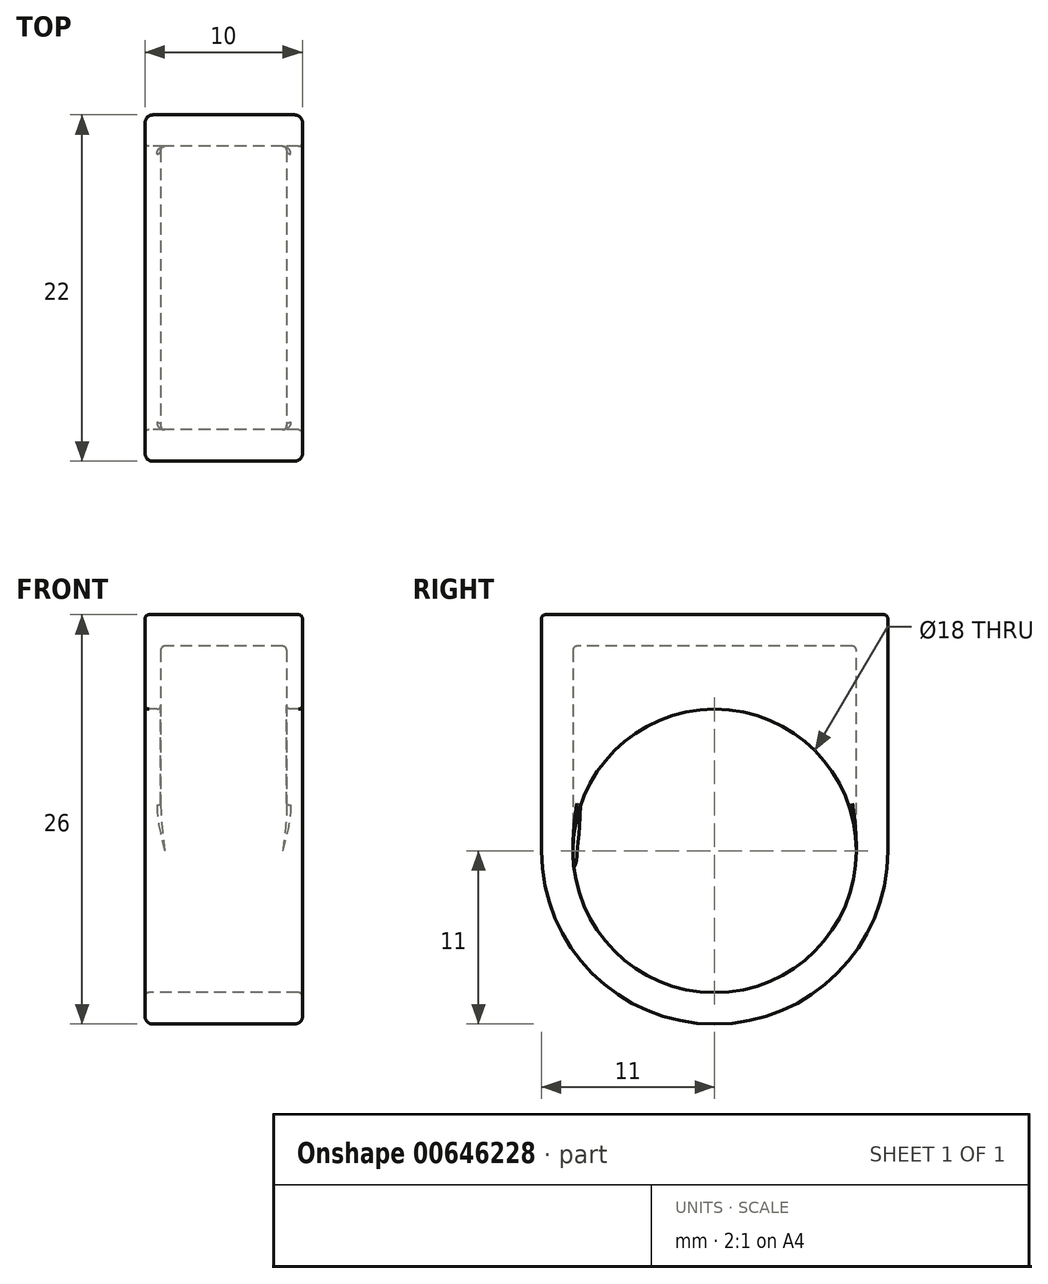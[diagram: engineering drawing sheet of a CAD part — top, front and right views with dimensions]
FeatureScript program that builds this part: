
annotation { "Feature Type Name" : "Feature", "Feature Type Description" : "" }
export const myFeature = defineFeature(function(context is Context, id is Id, definition is map)
    precondition{}
    {
        {
            var Q0;
            Q0=qCreatedBy(makeId("Right.planeOp"),FACE);
            var sketch = newSketch(context, id + "F0", { "sketchPlane" : qUnion([Q0])});
            skCircle(sketch, "E0", {"center": v(0, 0) * mm, "radius": 9 * mm});
            skArc(sketch, "E1", {"start": v(-11, 0) * mm, "mid": v(0, -11) * mm, "end": v(11, 0) * mm});
            skLineSegment(sketch, "E2", {"start": v(-11, 0) * mm, "end": v(-11, 15) * mm});
            skLineSegment(sketch, "E3", {"start": v(11, 0) * mm, "end": v(11, 15) * mm});
            skLineSegment(sketch, "E4", {"start": v(-11, 15) * mm, "end": v(11, 15) * mm});
            skSolve(sketch);
        }
        {
            var Q0;
            Q0 = qSketchRegion(id + "F0", true);
            extrude(context, id + "F1", {"entities" : qUnion([Q0]), "endBound" : BoundingType.SYMMETRIC, "depth" : 10 * mm, "offsetDistance" : 25 * mm});
        }
        {
            var Q0;
            Q0=qCreatedBy(makeId("Right.planeOp"),FACE);
            var sketch = newSketch(context, id + "F2", { "sketchPlane" : qUnion([Q0])});
            skLineSegment(sketch, "E5.0", {"start": v(9, 13) * mm, "end": v(-9, 13) * mm});
            skLineSegment(sketch, "E5.1", {"start": v(9, 0) * mm, "end": v(9, 13) * mm});
            skArc(sketch, "E5.2", {"start": v(-9, 0) * mm, "mid": v(0, -9) * mm, "end": v(9, 0) * mm});
            skLineSegment(sketch, "E5.3", {"start": v(-9, 13) * mm, "end": v(-9, 0) * mm});
            skSolve(sketch);
        }
        {
            var Q0;
            Q0 = qSketchRegion(id + "F2", true);
            extrude(context, id + "F3", {"entities" : qUnion([Q0]), "operationType" : NewBodyOperationType.REMOVE, "endBound" : BoundingType.SYMMETRIC, "depth" : 8 * mm, "offsetDistance" : 25 * mm});
        }
        {
            var Q0;
            Q0=makeQuery(id+"F1.opExtrude","CAP_EDGE",EDGE,{"disambiguationData":[OSD([sQuery(id+"F0.wireOp",EDGE,"E2")])],"isStart":true});
            var Q1;
            Q1=makeQuery(id+"F1.opExtrude","CAP_EDGE",EDGE,{"disambiguationData":[OSD([sQuery(id+"F0.wireOp",EDGE,"E2")])],"isStart":false});
            fillet(context, id + "F4", {"entities" : qUnion([Q0, Q1]), "radius" : 0.5 * mm, "tangentPropagation" : true, "allowEdgeOverflow" : false});
        }
        {
            var Q0;
            Q0=makeQuery(id+"F1.opExtrude","CAP_EDGE",EDGE,{"disambiguationData":[OSD([sQuery(id+"F0.wireOp",EDGE,"E0")])],"isStart":false});
            var Q1;
            Q1=makeQuery(id+"F1.opExtrude","CAP_FACE",FACE,{"disambiguationData":[OSD([sQuery(id+"F0.wireOp",EDGE,"E0"),sQuery(id+"F0.wireOp",EDGE,"E1"),sQuery(id+"F0.wireOp",EDGE,"E2"),sQuery(id+"F0.wireOp",EDGE,"E3"),sQuery(id+"F0.wireOp",EDGE,"E4")])],"isStart":false});
            var Q2;
            Q2=makeQuery(id+"F1.opExtrude","CAP_FACE",FACE,{"disambiguationData":[OSD([sQuery(id+"F0.wireOp",EDGE,"E0"),sQuery(id+"F0.wireOp",EDGE,"E1"),sQuery(id+"F0.wireOp",EDGE,"E2"),sQuery(id+"F0.wireOp",EDGE,"E3"),sQuery(id+"F0.wireOp",EDGE,"E4")])],"isStart":true});
            var Q3;
            Q3=makeQuery(id+"F1.opExtrude","SWEPT_FACE",FACE,{"disambiguationData":[OSD([sQuery(id+"F0.wireOp",EDGE,"E2")])]});
            var Q4;
            Q4=makeQuery(id+"F1.opExtrude","SWEPT_EDGE",EDGE,{"disambiguationData":[OSD([sQuery(id+"F0.wireOp",EDGE,"E3"),sQuery(id+"F0.wireOp",EDGE,"E4")])]});
            var Q5;
            Q5=makeQuery(id+"F1.opExtrude","SWEPT_EDGE",EDGE,{"disambiguationData":[OSD([sQuery(id+"F0.wireOp",EDGE,"E1"),sQuery(id+"F0.wireOp",EDGE,"E2")])]});
            var Q6;
            Q6=makeQuery(id+"F1.opExtrude","SWEPT_EDGE",EDGE,{"disambiguationData":[OSD([sQuery(id+"F0.wireOp",EDGE,"E2"),sQuery(id+"F0.wireOp",EDGE,"E4")])]});
            var Q7;
            Q7=makeQuery(id+"F1.opExtrude","CAP_EDGE",EDGE,{"disambiguationData":[OSD([sQuery(id+"F0.wireOp",EDGE,"E4")])],"isStart":false});
            var Q8;
            Q8=makeQuery(id+"F1.opExtrude","CAP_EDGE",EDGE,{"disambiguationData":[OSD([sQuery(id+"F0.wireOp",EDGE,"E0")])],"isStart":true});
            var Q9;
            Q9=makeQuery(id+"F1.opExtrude","SWEPT_FACE",FACE,{"disambiguationData":[OSD([sQuery(id+"F0.wireOp",EDGE,"E1")])]});
            var Q10;
            Q10=makeQuery(id+"F1.opExtrude","SWEPT_FACE",FACE,{"disambiguationData":[OSD([sQuery(id+"F0.wireOp",EDGE,"E3")])]});
            var Q11;
            Q11=makeQuery(id+"F1.opExtrude","CAP_EDGE",EDGE,{"disambiguationData":[OSD([sQuery(id+"F0.wireOp",EDGE,"E1")])],"isStart":true});
            var Q12;
            Q12=makeQuery(id+"F1.opExtrude","SWEPT_FACE",FACE,{"disambiguationData":[OSD([sQuery(id+"F0.wireOp",EDGE,"E4")])]});
            var Q13;
            Q13=makeQuery(id+"F1.opExtrude","CAP_EDGE",EDGE,{"disambiguationData":[OSD([sQuery(id+"F0.wireOp",EDGE,"E1")])],"isStart":false});
            var Q14;
            Q14=makeQuery(id+"F1.opExtrude","CAP_EDGE",EDGE,{"disambiguationData":[OSD([sQuery(id+"F0.wireOp",EDGE,"E2")])],"isStart":true});
            var Q15;
            Q15=makeQuery(id+"F1.opExtrude","CAP_EDGE",EDGE,{"disambiguationData":[OSD([sQuery(id+"F0.wireOp",EDGE,"E2")])],"isStart":false});
            var Q16;
            Q16=makeQuery(id+"F1.opExtrude","CAP_EDGE",EDGE,{"disambiguationData":[OSD([sQuery(id+"F0.wireOp",EDGE,"E3")])],"isStart":false});
            var Q17;
            Q17=makeQuery(id+"F1.opExtrude","CAP_EDGE",EDGE,{"disambiguationData":[OSD([sQuery(id+"F0.wireOp",EDGE,"E4")])],"isStart":true});
            var Q18;
            Q18=makeQuery(id+"F3.boolean.opBoolean","COPY",EDGE,{"derivedFrom":makeQuery(id+"F3.opExtrude","SWEPT_EDGE",EDGE,{"disambiguationData":[OSD([sQuery(id+"F2.wireOp",EDGE,"E5.1"),sQuery(id+"F2.wireOp",EDGE,"E5.2")])]})});
            var Q19;
            Q19=makeQuery(id+"F3.boolean.opBoolean","COPY",FACE,{"derivedFrom":makeQuery(id+"F3.opExtrude","SWEPT_FACE",FACE,{"disambiguationData":[OSD([sQuery(id+"F2.wireOp",EDGE,"E5.1")])]})});
            var Q20;
            Q20=makeQuery(id+"F1.opExtrude","SWEPT_FACE",FACE,{"disambiguationData":[OSD([sQuery(id+"F0.wireOp",EDGE,"E0")])]});
            var Q21;
            Q21=makeQuery(id+"F1.opExtrude","SWEPT_EDGE",EDGE,{"disambiguationData":[OSD([sQuery(id+"F0.wireOp",EDGE,"E1"),sQuery(id+"F0.wireOp",EDGE,"E3")])]});
            var Q22;
            Q22=makeQuery(id+"F1.opExtrude","CAP_EDGE",EDGE,{"disambiguationData":[OSD([sQuery(id+"F0.wireOp",EDGE,"E3")])],"isStart":true});
            var Q23;
            Q23=makeQuery(id+"F3.boolean.opBoolean","COPY",EDGE,{"derivedFrom":makeQuery(id+"F3.opExtrude","SWEPT_EDGE",EDGE,{"disambiguationData":[OSD([sQuery(id+"F2.wireOp",EDGE,"E5.0"),sQuery(id+"F2.wireOp",EDGE,"E5.1")])]})});
            var Q24;
            Q24=makeQuery(id+"F3.boolean.opBoolean","COPY",FACE,{"derivedFrom":makeQuery(id+"F3.opExtrude","SWEPT_FACE",FACE,{"disambiguationData":[OSD([sQuery(id+"F2.wireOp",EDGE,"E5.0")])]})});
            var Q25;
            Q25=makeQuery(id+"F3.boolean.opBoolean","COPY",EDGE,{"derivedFrom":makeQuery(id+"F3.opExtrude","SWEPT_EDGE",EDGE,{"disambiguationData":[OSD([sQuery(id+"F2.wireOp",EDGE,"E5.0"),sQuery(id+"F2.wireOp",EDGE,"E5.3")])]})});
            var Q26;
            Q26=makeQuery(id+"F3.boolean.opBoolean","COPY",FACE,{"derivedFrom":makeQuery(id+"F3.opExtrude","CAP_FACE",FACE,{"disambiguationData":[OSD([sQuery(id+"F2.wireOp",EDGE,"E5.0"),sQuery(id+"F2.wireOp",EDGE,"E5.1"),sQuery(id+"F2.wireOp",EDGE,"E5.2"),sQuery(id+"F2.wireOp",EDGE,"E5.3")])],"isStart":true})});
            var Q27;
            Q27=makeQuery(id+"F3.boolean.opBoolean","COPY",FACE,{"derivedFrom":makeQuery(id+"F3.opExtrude","CAP_FACE",FACE,{"disambiguationData":[OSD([sQuery(id+"F2.wireOp",EDGE,"E5.0"),sQuery(id+"F2.wireOp",EDGE,"E5.1"),sQuery(id+"F2.wireOp",EDGE,"E5.2"),sQuery(id+"F2.wireOp",EDGE,"E5.3")])],"isStart":false})});
            var Q28;
            Q28=makeQuery(id+"F3.boolean.opBoolean","COPY",EDGE,{"derivedFrom":makeQuery(id+"F3.opExtrude","SWEPT_EDGE",EDGE,{"disambiguationData":[OSD([sQuery(id+"F2.wireOp",EDGE,"E5.2"),sQuery(id+"F2.wireOp",EDGE,"E5.3")])]})});
            var Q29;
            Q29=makeQuery(id+"F3.boolean.opBoolean","COPY",EDGE,{"derivedFrom":makeQuery(id+"F3.opExtrude","CAP_EDGE",EDGE,{"disambiguationData":[OSD([sQuery(id+"F2.wireOp",EDGE,"E5.0")])],"isStart":true})});
            var Q30;
            Q30=makeQuery(id+"F3.boolean.opBoolean","COPY",FACE,{"derivedFrom":makeQuery(id+"F3.opExtrude","SWEPT_FACE",FACE,{"disambiguationData":[OSD([sQuery(id+"F2.wireOp",EDGE,"E5.3")])]})});
            var Q31;
            Q31=makeQuery(id+"F3.boolean.opBoolean","COPY",EDGE,{"derivedFrom":makeQuery(id+"F3.opExtrude","CAP_EDGE",EDGE,{"disambiguationData":[OSD([sQuery(id+"F2.wireOp",EDGE,"E5.0")])],"isStart":false})});
            var Q32;
            Q32=makeQuery(id+"F3.boolean.opBoolean","COPY",EDGE,{"derivedFrom":makeQuery(id+"F3.opExtrude","CAP_EDGE",EDGE,{"disambiguationData":[OSD([sQuery(id+"F2.wireOp",EDGE,"E5.1")])],"isStart":false})});
            var Q33;
            Q33=makeQuery(id+"F3.boolean.opBoolean","COPY",EDGE,{"derivedFrom":makeQuery(id+"F3.opExtrude","CAP_EDGE",EDGE,{"disambiguationData":[OSD([sQuery(id+"F2.wireOp",EDGE,"E5.3")])],"isStart":true})});
            var Q34;
            Q34=makeQuery(id+"F3.boolean.opBoolean","COPY",EDGE,{"derivedFrom":makeQuery(id+"F3.opExtrude","CAP_EDGE",EDGE,{"disambiguationData":[OSD([sQuery(id+"F2.wireOp",EDGE,"E5.3")])],"isStart":false})});
            var Q35;
            Q35=makeQuery(id+"F3.boolean.opBoolean","INTERSECT",EDGE,{"derivedFrom":[makeQuery(id+"F1.opExtrude","SWEPT_FACE",FACE,{"disambiguationData":[OSD([sQuery(id+"F0.wireOp",EDGE,"E0")])]}),makeQuery(id+"F3.opExtrude","CAP_FACE",FACE,{"disambiguationData":[OSD([sQuery(id+"F2.wireOp",EDGE,"E5.0"),sQuery(id+"F2.wireOp",EDGE,"E5.1"),sQuery(id+"F2.wireOp",EDGE,"E5.2"),sQuery(id+"F2.wireOp",EDGE,"E5.3")])],"isStart":false})]});
            var Q36;
            Q36=makeQuery(id+"F3.boolean.opBoolean","COPY",EDGE,{"derivedFrom":makeQuery(id+"F3.opExtrude","CAP_EDGE",EDGE,{"disambiguationData":[OSD([sQuery(id+"F2.wireOp",EDGE,"E5.1")])],"isStart":true})});
            var Q37;
            Q37=makeQuery(id+"F3.boolean.opBoolean","INTERSECT",EDGE,{"derivedFrom":[makeQuery(id+"F1.opExtrude","SWEPT_FACE",FACE,{"disambiguationData":[OSD([sQuery(id+"F0.wireOp",EDGE,"E0")])]}),makeQuery(id+"F3.opExtrude","CAP_FACE",FACE,{"disambiguationData":[OSD([sQuery(id+"F2.wireOp",EDGE,"E5.0"),sQuery(id+"F2.wireOp",EDGE,"E5.1"),sQuery(id+"F2.wireOp",EDGE,"E5.2"),sQuery(id+"F2.wireOp",EDGE,"E5.3")])],"isStart":true})]});
            fillet(context, id + "F5", {"entities" : qUnion([Q0, Q1, Q2, Q3, Q4, Q5, Q6, Q7, Q8, Q9, Q10, Q11, Q12, Q13, Q14, Q15, Q16, Q17, Q18, Q19, Q20, Q21, Q22, Q23, Q24, Q25, Q26, Q27, Q28, Q29, Q30, Q31, Q32, Q33, Q34, Q35, Q36, Q37]), "radius" : .25 * mm, "tangentPropagation" : true, "allowEdgeOverflow" : false});
        }
    });
